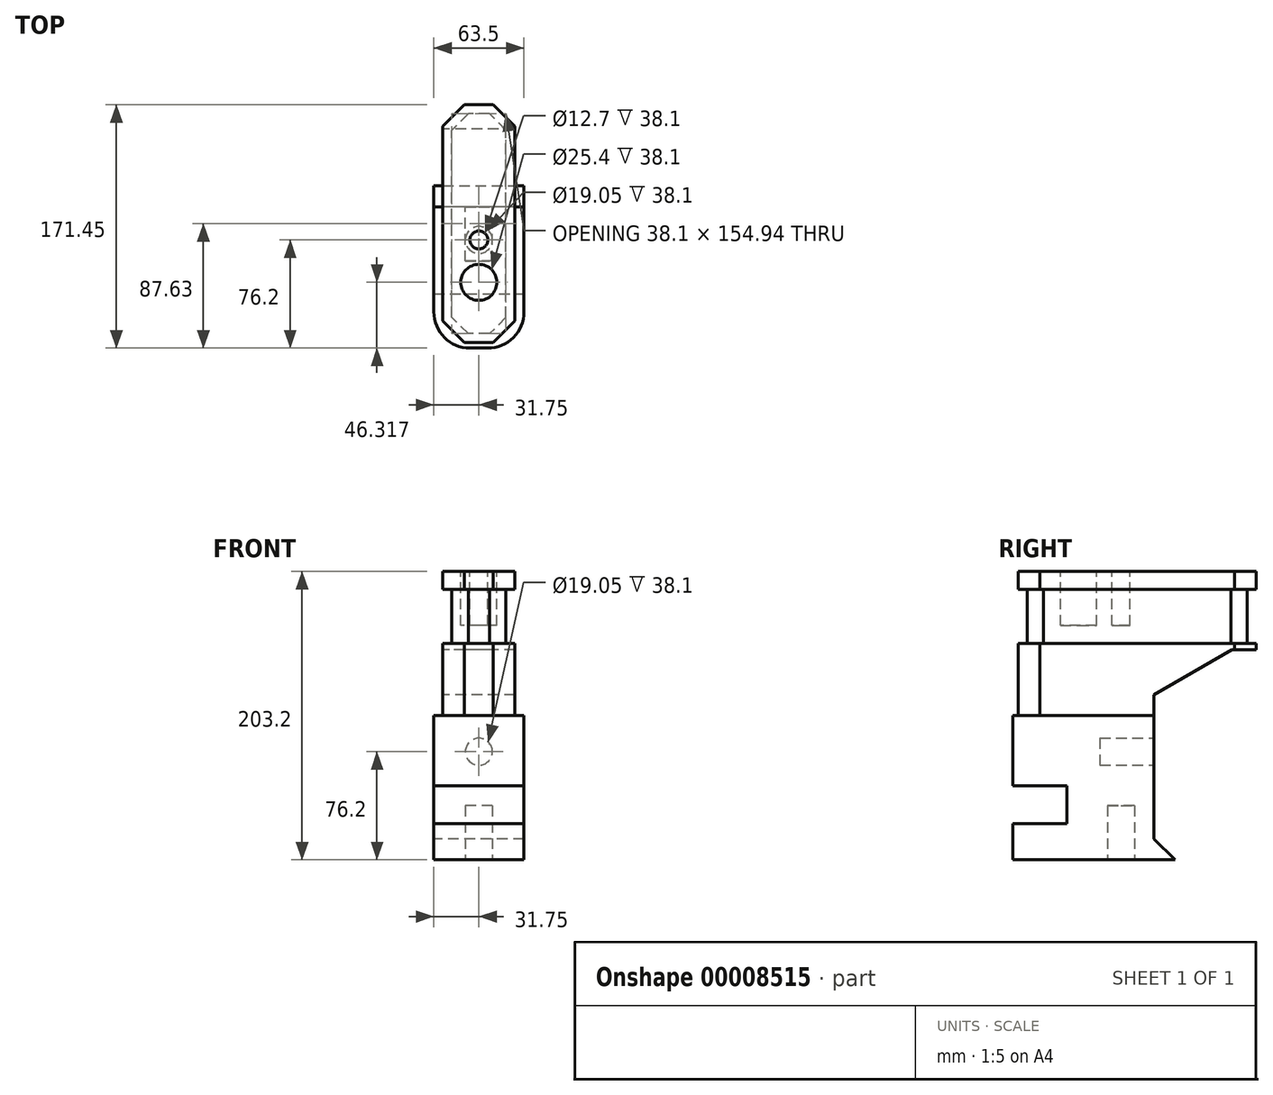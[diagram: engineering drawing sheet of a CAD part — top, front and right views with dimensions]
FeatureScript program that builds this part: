
annotation { "Feature Type Name" : "Feature", "Feature Type Description" : "" }
export const myFeature = defineFeature(function(context is Context, id is Id, definition is map)
    precondition{}
    {
        {
            var Q0;
            Q0=qCreatedBy(makeId("Top.planeOp"),FACE);
            var sketch = newSketch(context, id + "F0", { "sketchPlane" : qUnion([Q0])});
            skCircle(sketch, "E0", {"center": v(0, 0) * mm, "radius": 9.53 * mm});
            skSolve(sketch);
        }
        {
            var Q0;
            Q0=makeQuery(id+"F0.imprint","IMPRINT",FACE,{"disambiguationData":[TD([[makeQuery(id+"F0.imprint","IMPRINT",EDGE,{"derivedFrom":sQuery(id+"F0.wireOp",EDGE,"E0")}),1.0]])]});
            extrude(context, id + "F1", {"entities" : qUnion([Q0]), "depth" : 38.1 * mm});
        }
        {
            var Q0;
            Q0=makeQuery(id+"F1.opExtrude","CAP_FACE",FACE,{"disambiguationData":[OSD([sQuery(id+"F0.wireOp",EDGE,"E0")])],"isStart":false});
            var sketch = newSketch(context, id + "F2", { "sketchPlane" : qUnion([Q0])});
            skLineSegment(sketch, "E1.bottom", {"start": v(-31.75, -76.2) * mm, "end": v(31.75, -76.2) * mm});
            skLineSegment(sketch, "E1.top", {"start": v(-31.75, 38.1) * mm, "end": v(31.75, 38.1) * mm});
            skLineSegment(sketch, "E1.left", {"start": v(-31.75, -76.2) * mm, "end": v(-31.75, 38.1) * mm});
            skLineSegment(sketch, "E1.right", {"start": v(31.75, -76.2) * mm, "end": v(31.75, 38.1) * mm});
            skSolve(sketch);
        }
        {
            var Q0;
            Q0=makeQuery(id+"F2.imprint","IMPRINT",FACE,{"disambiguationData":[TD([[makeQuery(id+"F2.imprint","IMPRINT",EDGE,{"derivedFrom":sQuery(id+"F2.wireOp",EDGE,"E1.bottom")}),1.0]])]});
            var Q1;
            Q1=makeQuery(id+"F2.imprint","IMPRINT",FACE,{"disambiguationData":[TD([[makeQuery(id+"F2.imprint","IMPRINT",EDGE,{"derivedFrom":makeQuery(id+"F1.opExtrude","CAP_EDGE",EDGE,{"disambiguationData":[OSD([sQuery(id+"F0.wireOp",EDGE,"E0")])],"isStart":false})}),1.0]])]});
            extrude(context, id + "F3", {"entities" : qUnion([Q0, Q1]), "operationType" : NewBodyOperationType.ADD, "depth" : 101.6 * mm});
        }
        {
            var Q0;
            Q0=makeQuery(id+"F3.opExtrude","SWEPT_EDGE",EDGE,{"disambiguationData":[OSD([sQuery(id+"F2.wireOp",EDGE,"E1.bottom"),sQuery(id+"F2.wireOp",EDGE,"E1.right")])]});
            var Q1;
            Q1=makeQuery(id+"F3.opExtrude","SWEPT_EDGE",EDGE,{"disambiguationData":[OSD([sQuery(id+"F2.wireOp",EDGE,"E1.bottom"),sQuery(id+"F2.wireOp",EDGE,"E1.left")])]});
            fillet(context, id + "F4", {"entities" : qUnion([Q0, Q1]), "radius" : 25.4 * mm, "tangentPropagation" : true, "allowEdgeOverflow" : false});
        }
        {
            var Q0;
            Q0=makeQuery(id+"F3.opExtrude","CAP_FACE",FACE,{"disambiguationData":[OSD([sQuery(id+"F2.wireOp",EDGE,"E1.bottom"),sQuery(id+"F2.wireOp",EDGE,"E1.top"),sQuery(id+"F2.wireOp",EDGE,"E1.left"),sQuery(id+"F2.wireOp",EDGE,"E1.right")])],"isStart":false});
            var sketch = newSketch(context, id + "F5", { "sketchPlane" : qUnion([Q0])});
            skLineSegment(sketch, "E2.bottom", {"start": v(25.4, -57.15) * mm, "end": v(-25.4, -57.15) * mm});
            skLineSegment(sketch, "E2.top", {"start": v(10.16, 95.25) * mm, "end": v(-10.16, 95.25) * mm});
            skLineSegment(sketch, "E2.left", {"start": v(25.4, -57.15) * mm, "end": v(25.4, 80) * mm});
            skLineSegment(sketch, "E2.right", {"start": v(-25.4, -57.15) * mm, "end": v(-25.4, 80) * mm});
            skLineSegment(sketch, "E3", {"start": v(25.4, -57.15) * mm, "end": v(10.16, -72.4) * mm});
            skLineSegment(sketch, "E4", {"start": v(10.16, -72.4) * mm, "end": v(-10.16, -72.4) * mm});
            skLineSegment(sketch, "E5", {"start": v(-10.16, -72.4) * mm, "end": v(-25.4, -57.15) * mm});
            skLineSegment(sketch, "E6", {"start": v(25.4, 80) * mm, "end": v(10.16, 95.25) * mm});
            skLineSegment(sketch, "E7", {"start": v(-10.16, 95.25) * mm, "end": v(-25.4, 80) * mm});
            skPoint(sketch, "E8.orphan", {"position": v(-25.4, 95.25) * mm});
            skSolve(sketch);
        }
        {
            var Q0;
            Q0 = qSketchRegion(id + "F5", true);
            extrude(context, id + "F6", {"entities" : qUnion([Q0]), "operationType" : NewBodyOperationType.ADD, "depth" : 101.6 * mm});
        }
        {
            var Q0;
            Q0=qCreatedBy(makeId("Top.planeOp"),FACE);
            cPlane(context, id + "F7", {"entities" : qUnion([Q0]), "cplaneType" : CPlaneType.OFFSET, "offset" : 190.5 * mm, "width" : 152.4 * mm, "height" : 152.4 * mm});
        }
        {
            var Q0;
            Q0=qCreatedBy(id+"F7.planeOp",FACE);
            var sketch = newSketch(context, id + "F8", { "sketchPlane" : qUnion([Q0])});
            skLineSegment(sketch, "E9.0", {"start": v(-7.53, -66.04) * mm, "end": v(-19.05, -54.52) * mm});
            skLineSegment(sketch, "E9.1", {"start": v(7.53, -66.04) * mm, "end": v(-7.53, -66.04) * mm});
            skLineSegment(sketch, "E9.2", {"start": v(19.05, -54.52) * mm, "end": v(7.53, -66.04) * mm});
            skLineSegment(sketch, "E9.3", {"start": v(19.05, -54.52) * mm, "end": v(19.05, 77.38) * mm});
            skLineSegment(sketch, "E9.4", {"start": v(19.05, 77.38) * mm, "end": v(7.53, 88.9) * mm});
            skLineSegment(sketch, "E9.5", {"start": v(-19.05, -54.52) * mm, "end": v(-19.05, 77.38) * mm});
            skLineSegment(sketch, "E9.6", {"start": v(7.53, 88.9) * mm, "end": v(-7.53, 88.9) * mm});
            skLineSegment(sketch, "E9.7", {"start": v(-7.53, 88.9) * mm, "end": v(-19.05, 77.38) * mm});
            skLineSegment(sketch, "E10.0", {"start": v(-10.16, -72.4) * mm, "end": v(10.16, -72.4) * mm});
            skLineSegment(sketch, "E10.1", {"start": v(-25.4, -57.15) * mm, "end": v(-10.16, -72.4) * mm});
            skLineSegment(sketch, "E10.2", {"start": v(-25.4, 80) * mm, "end": v(-25.4, -57.15) * mm});
            skLineSegment(sketch, "E10.3", {"start": v(-10.16, 95.25) * mm, "end": v(-25.4, 80) * mm});
            skLineSegment(sketch, "E10.4", {"start": v(10.16, 95.25) * mm, "end": v(-10.16, 95.25) * mm});
            skLineSegment(sketch, "E10.5", {"start": v(10.16, -72.4) * mm, "end": v(25.4, -57.15) * mm});
            skLineSegment(sketch, "E10.6", {"start": v(25.4, 80.01) * mm, "end": v(10.16, 95.25) * mm});
            skLineSegment(sketch, "E10.7", {"start": v(25.4, -57.15) * mm, "end": v(25.4, 80.01) * mm});
            skSolve(sketch);
        }
        {
            var Q0;
            Q0=makeQuery(id+"F8.imprint","IMPRINT",FACE,{"disambiguationData":[TD([[makeQuery(id+"F8.imprint","IMPRINT",EDGE,{"derivedFrom":sQuery(id+"F8.wireOp",EDGE,"E9.0")}),1.0]])]});
            extrude(context, id + "F9", {"entities" : qUnion([Q0]), "operationType" : NewBodyOperationType.REMOVE, "depth" : 38.1 * mm});
        }
        {
            var Q0;
            Q0=qCreatedBy(makeId("Right.planeOp"),FACE);
            var sketch = newSketch(context, id + "F10", { "sketchPlane" : qUnion([Q0])});
            skLineSegment(sketch, "E11.0", {"start": v(38.1, 139.7) * mm, "end": v(38.1, 38.1) * mm});
            skLineSegment(sketch, "E11.1", {"start": v(-50.8, 38.1) * mm, "end": v(38.1, 38.1) * mm});
            skLineSegment(sketch, "E11.2", {"start": v(-50.8, 139.7) * mm, "end": v(38.1, 139.7) * mm});
            skLineSegment(sketch, "E12", {"start": v(38.1, 38.1) * mm, "end": v(23.22, 52.98) * mm});
            skLineSegment(sketch, "E13", {"start": v(23.22, 52.98) * mm, "end": v(23.22, 154.58) * mm});
            skLineSegment(sketch, "E14", {"start": v(23.22, 154.58) * mm, "end": v(78.2, 186.33) * mm});
            skLineSegment(sketch, "E15", {"start": v(38.1, 38.1) * mm, "end": v(127, 38.1) * mm});
            skLineSegment(sketch, "E16", {"start": v(78.2, 186.33) * mm, "end": v(116.3, 186.33) * mm});
            skLineSegment(sketch, "E17", {"start": v(116.3, 186.33) * mm, "end": v(419.95, 159.77) * mm});
            skLineSegment(sketch, "E18", {"start": v(419.95, 159.77) * mm, "end": v(523.54, 111.46) * mm});
            skLineSegment(sketch, "E19", {"start": v(127, 38.1) * mm, "end": v(165.5, 60.32) * mm});
            skLineSegment(sketch, "E20", {"start": v(365.08, 0.26) * mm, "end": v(421.84, -9.74) * mm});
            skLineSegment(sketch, "E21", {"start": v(421.84, -9.74) * mm, "end": v(523.54, 111.46) * mm});
            skLineSegment(sketch, "E22", {"start": v(365.08, 0.26) * mm, "end": v(340.6, 29.45) * mm});
            skLineSegment(sketch, "E23", {"start": v(165.5, 60.33) * mm, "end": v(340.6, 29.45) * mm});
            skSolve(sketch);
        }
        {
            var Q0;
            Q0 = qSketchRegion(id + "F10", true);
            extrude(context, id + "F11", {"entities" : qUnion([Q0]), "operationType" : NewBodyOperationType.REMOVE, "depth" : 88.9 * mm, "symmetric" : true});
        }
        {
            var Q0;
            Q0=makeQuery(id+"F3.opExtrude","SWEPT_FACE",FACE,{"disambiguationData":[OSD([sQuery(id+"F2.wireOp",EDGE,"E1.right")])]});
            var sketch = newSketch(context, id + "F12", { "sketchPlane" : qUnion([Q0])});
            skLineSegment(sketch, "E24.bottom", {"start": v(-38.1, 63.5) * mm, "end": v(-88.9, 63.5) * mm});
            skLineSegment(sketch, "E24.top", {"start": v(-38.1, 90.17) * mm, "end": v(-88.9, 90.17) * mm});
            skLineSegment(sketch, "E24.left", {"start": v(-38.1, 63.5) * mm, "end": v(-38.1, 90.17) * mm});
            skLineSegment(sketch, "E24.right", {"start": v(-88.9, 63.5) * mm, "end": v(-88.9, 90.17) * mm});
            skSolve(sketch);
        }
        {
            var Q0;
            {var subQ6=sQuery(id+"F12.wireOp",EDGE,"E24.right");Q0=makeQuery(id+"F12.imprint","IMPRINT",FACE,{"disambiguationData":[TD([[makeQuery(id+"F12.imprint","IMPRINT",EDGE,{"derivedFrom":subQ6}),-1.0]])]});}
            var Q1;
            {var subQ6=sQuery(id+"F12.wireOp",EDGE,"E24.left");Q1=makeQuery(id+"F12.imprint","IMPRINT",FACE,{"disambiguationData":[TD([[makeQuery(id+"F12.imprint","IMPRINT",EDGE,{"derivedFrom":subQ6}),1.0]])]});}
            extrude(context, id + "F13", {"entities" : qUnion([Q0, Q1]), "operationType" : NewBodyOperationType.REMOVE, "oppositeDirection" : true, "depth" : 76.2 * mm});
        }
        {
            var Q0;
            Q0=makeQuery(id+"F11.boolean.opBoolean","COPY",FACE,{"derivedFrom":makeQuery(id+"F11.opExtrude","SWEPT_FACE",FACE,{"disambiguationData":[OSD([sQuery(id+"F10.wireOp",EDGE,"E13")])]})});
            var sketch = newSketch(context, id + "F14", { "sketchPlane" : qUnion([Q0])});
            skCircle(sketch, "E25", {"center": v(0, 114.3) * mm, "radius": 9.53 * mm});
            skSolve(sketch);
        }
        {
            var Q0;
            Q0=makeQuery(id+"F14.imprint","IMPRINT",FACE,{"disambiguationData":[TD([[makeQuery(id+"F14.imprint","IMPRINT",EDGE,{"derivedFrom":sQuery(id+"F14.wireOp",EDGE,"E25")}),1.0]])]});
            extrude(context, id + "F15", {"entities" : qUnion([Q0]), "operationType" : NewBodyOperationType.REMOVE, "oppositeDirection" : true, "depth" : 38.1 * mm});
        }
        {
            var Q0;
            Q0=makeQuery(id+"F6.opExtrude","CAP_FACE",FACE,{"disambiguationData":[OSD([sQuery(id+"F5.wireOp",EDGE,"E2.top"),sQuery(id+"F5.wireOp",EDGE,"E2.left"),sQuery(id+"F5.wireOp",EDGE,"E2.right"),sQuery(id+"F5.wireOp",EDGE,"E3"),sQuery(id+"F5.wireOp",EDGE,"E4"),sQuery(id+"F5.wireOp",EDGE,"E5"),sQuery(id+"F5.wireOp",EDGE,"E6"),sQuery(id+"F5.wireOp",EDGE,"E7")])],"isStart":false});
            var sketch = newSketch(context, id + "F16", { "sketchPlane" : qUnion([Q0])});
            skCircle(sketch, "E26", {"center": v(0, -29.88) * mm, "radius": 12.7 * mm});
            skCircle(sketch, "E27", {"center": v(0, 0) * mm, "radius": 6.35 * mm});
            skSolve(sketch);
        }
        {
            var Q0;
            Q0=makeQuery(id+"F16.imprint","IMPRINT",FACE,{"disambiguationData":[TD([[makeQuery(id+"F16.imprint","IMPRINT",EDGE,{"derivedFrom":sQuery(id+"F16.wireOp",EDGE,"E26")}),1.0]])]});
            var Q1;
            Q1=makeQuery(id+"F16.imprint","IMPRINT",FACE,{"disambiguationData":[TD([[makeQuery(id+"F16.imprint","IMPRINT",EDGE,{"derivedFrom":sQuery(id+"F16.wireOp",EDGE,"E27")}),1.0]])]});
            extrude(context, id + "F17", {"entities" : qUnion([Q0, Q1]), "operationType" : NewBodyOperationType.REMOVE, "oppositeDirection" : true, "depth" : 38.1 * mm});
        }
        {
            var Q0;
            Q0=makeQuery(id+"F1.opExtrude","CAP_FACE",FACE,{"disambiguationData":[OSD([sQuery(id+"F0.wireOp",EDGE,"E0")])],"isStart":true});
            extrude(context, id + "F18", {"entities" : qUnion([Q0]), "operationType" : NewBodyOperationType.REMOVE, "oppositeDirection" : true, "depth" : 76.2 * mm});
        }
    });
